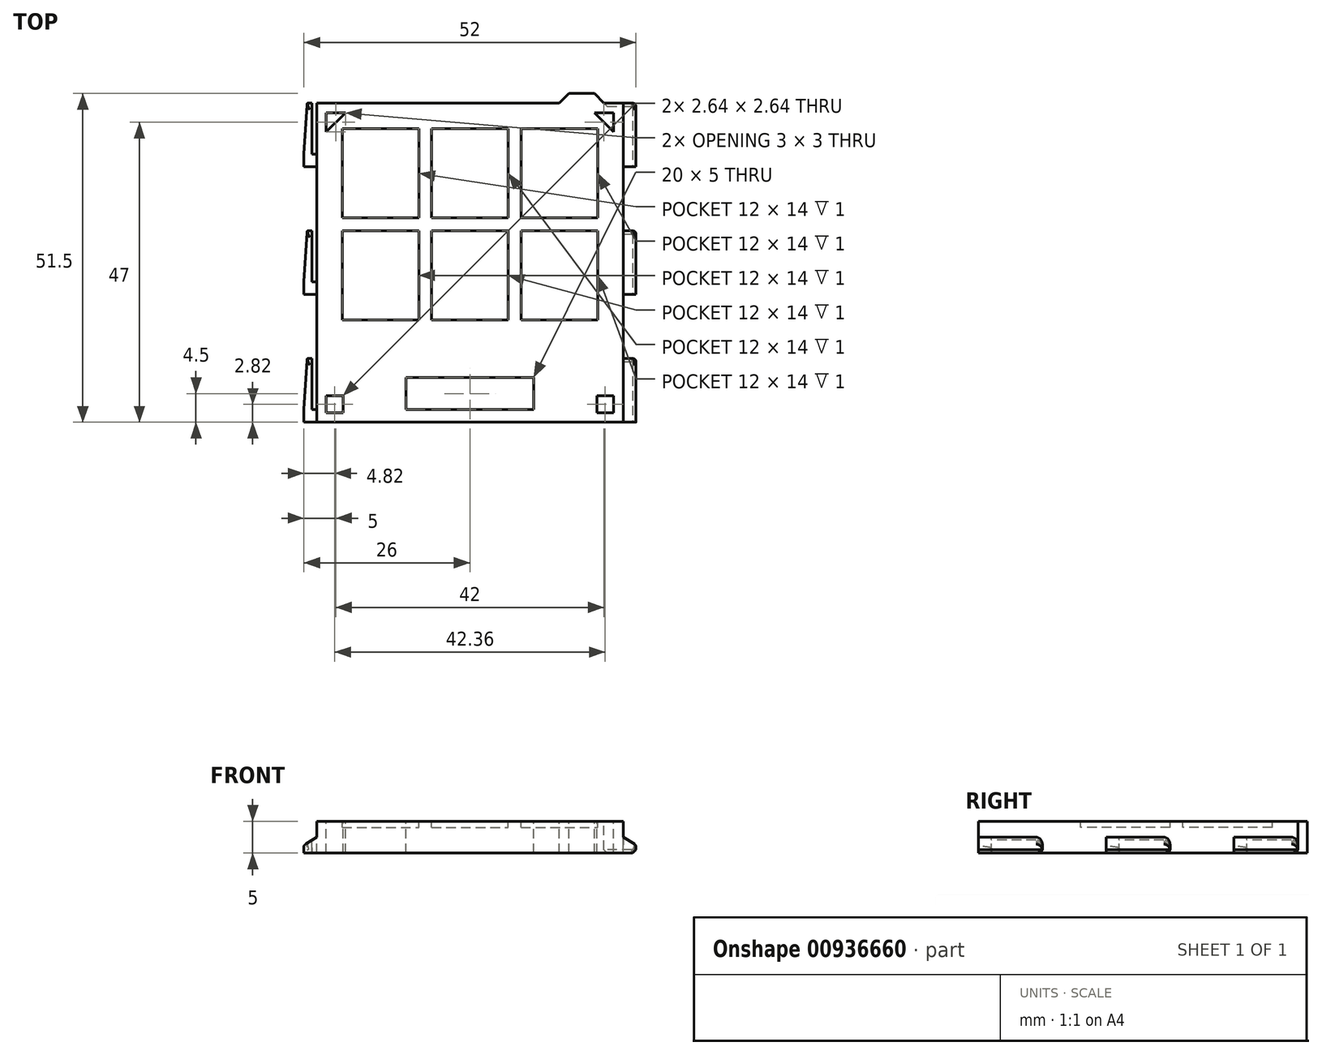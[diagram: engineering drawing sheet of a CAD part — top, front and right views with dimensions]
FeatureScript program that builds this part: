
annotation { "Feature Type Name" : "Feature", "Feature Type Description" : "" }
export const myFeature = defineFeature(function(context is Context, id is Id, definition is map)
    precondition{}
    {
        {
            var Q0;
            Q0=qCreatedBy(makeId("Top.planeOp"),FACE);
            var sketch = newSketch(context, id + "F0", { "sketchPlane" : qUnion([Q0])});
            skLineSegment(sketch, "E0.bottom", {"start": v(0, 0) * mm, "end": v(48, 0) * mm});
            skLineSegment(sketch, "E0.top", {"start": v(0, -50) * mm, "end": v(48, -50) * mm});
            skLineSegment(sketch, "E0.left", {"start": v(0, 0) * mm, "end": v(0, -50) * mm});
            skLineSegment(sketch, "E0.right", {"start": v(48, 0) * mm, "end": v(48, -50) * mm});
            skSolve(sketch);
        }
        {
            var Q0;
            Q0=makeQuery(id+"F0.imprint","IMPRINT",FACE,{"disambiguationData":[TD([[makeQuery(id+"F0.imprint","IMPRINT",EDGE,{"derivedFrom":sQuery(id+"F0.wireOp",EDGE,"E0.bottom")}),-1.0]])]});
            extrude(context, id + "F1", {"entities" : qUnion([Q0]), "depth" : 5 * mm, "offsetDistance" : 25 * mm});
        }
        {
            var Q0;
            Q0=makeQuery(id+"F1.opExtrude","CAP_FACE",FACE,{"disambiguationData":[OSD([sQuery(id+"F0.wireOp",EDGE,"E0.bottom"),sQuery(id+"F0.wireOp",EDGE,"E0.top"),sQuery(id+"F0.wireOp",EDGE,"E0.left"),sQuery(id+"F0.wireOp",EDGE,"E0.right")])],"isStart":false});
            var sketch = newSketch(context, id + "F2", { "sketchPlane" : qUnion([Q0])});
            skLineSegment(sketch, "E1.bottom", {"start": v(4, -4) * mm, "end": v(16, -4) * mm});
            skLineSegment(sketch, "E1.top", {"start": v(4, -18) * mm, "end": v(16, -18) * mm});
            skLineSegment(sketch, "E1.left", {"start": v(4, -4) * mm, "end": v(4, -18) * mm});
            skLineSegment(sketch, "E1.right", {"start": v(16, -4) * mm, "end": v(16, -18) * mm});
            skLineSegment(sketch, "E2.0.1.0", {"start": v(4, -34) * mm, "end": v(16, -34) * mm});
            skLineSegment(sketch, "E2.0.1.1", {"start": v(16, -20) * mm, "end": v(16, -34) * mm});
            skLineSegment(sketch, "E2.0.1.2", {"start": v(4, -20) * mm, "end": v(4, -34) * mm});
            skLineSegment(sketch, "E2.0.1.3", {"start": v(4, -20) * mm, "end": v(16, -20) * mm});
            skLineSegment(sketch, "E2.1.0.0", {"start": v(18, -18) * mm, "end": v(30, -18) * mm});
            skLineSegment(sketch, "E2.1.0.1", {"start": v(30, -4) * mm, "end": v(30, -18) * mm});
            skLineSegment(sketch, "E2.1.0.2", {"start": v(18, -4) * mm, "end": v(18, -18) * mm});
            skLineSegment(sketch, "E2.1.0.3", {"start": v(18, -4) * mm, "end": v(30, -4) * mm});
            skLineSegment(sketch, "E2.1.1.0", {"start": v(18, -34) * mm, "end": v(30, -34) * mm});
            skLineSegment(sketch, "E2.1.1.1", {"start": v(30, -20) * mm, "end": v(30, -34) * mm});
            skLineSegment(sketch, "E2.1.1.2", {"start": v(18, -20) * mm, "end": v(18, -34) * mm});
            skLineSegment(sketch, "E2.1.1.3", {"start": v(18, -20) * mm, "end": v(30, -20) * mm});
            skLineSegment(sketch, "E2.direction1", {"start": v(4, -18) * mm, "end": v(18, -18) * mm, "construction": true});
            skLineSegment(sketch, "E2.direction2", {"start": v(4, -18) * mm, "end": v(4, -34) * mm, "construction": true});
            skLineSegment(sketch, "E3.0.2.0", {"start": v(32, -18) * mm, "end": v(44, -18) * mm});
            skLineSegment(sketch, "E3.3.2.0", {"start": v(44, -4) * mm, "end": v(44, -18) * mm});
            skLineSegment(sketch, "E3.6.2.0", {"start": v(32, -4) * mm, "end": v(32, -18) * mm});
            skLineSegment(sketch, "E3.9.2.0", {"start": v(32, -4) * mm, "end": v(44, -4) * mm});
            skLineSegment(sketch, "E3.0.2.1", {"start": v(32, -34) * mm, "end": v(44, -34) * mm});
            skLineSegment(sketch, "E3.3.2.1", {"start": v(44, -20) * mm, "end": v(44, -34) * mm});
            skLineSegment(sketch, "E3.6.2.1", {"start": v(32, -20) * mm, "end": v(32, -34) * mm});
            skLineSegment(sketch, "E3.9.2.1", {"start": v(32, -20) * mm, "end": v(44, -20) * mm});
            skSolve(sketch);
        }
        {
            var Q0;
            Q0=makeQuery(id+"F2.imprint","IMPRINT",FACE,{"disambiguationData":[TD([[makeQuery(id+"F2.imprint","IMPRINT",EDGE,{"derivedFrom":sQuery(id+"F2.wireOp",EDGE,"E1.bottom")}),-1.0]])]});
            var Q1;
            Q1=makeQuery(id+"F2.imprint","IMPRINT",FACE,{"disambiguationData":[TD([[makeQuery(id+"F2.imprint","IMPRINT",EDGE,{"derivedFrom":sQuery(id+"F2.wireOp",EDGE,"E2.0.1.0")}),1.0]])]});
            var Q2;
            Q2=makeQuery(id+"F2.imprint","IMPRINT",FACE,{"disambiguationData":[TD([[makeQuery(id+"F2.imprint","IMPRINT",EDGE,{"derivedFrom":sQuery(id+"F2.wireOp",EDGE,"E2.0.2.0")}),1.0]])]});
            var Q3;
            Q3=makeQuery(id+"F2.imprint","IMPRINT",FACE,{"disambiguationData":[TD([[makeQuery(id+"F2.imprint","IMPRINT",EDGE,{"derivedFrom":sQuery(id+"F2.wireOp",EDGE,"E2.0.3.0")}),1.0]])]});
            var Q4;
            Q4=makeQuery(id+"F2.imprint","IMPRINT",FACE,{"disambiguationData":[TD([[makeQuery(id+"F2.imprint","IMPRINT",EDGE,{"derivedFrom":sQuery(id+"F2.wireOp",EDGE,"E2.2.0.0")}),1.0]])]});
            var Q5;
            Q5=makeQuery(id+"F2.imprint","IMPRINT",FACE,{"disambiguationData":[TD([[makeQuery(id+"F2.imprint","IMPRINT",EDGE,{"derivedFrom":sQuery(id+"F2.wireOp",EDGE,"E2.2.1.0")}),1.0]])]});
            var Q6;
            Q6=makeQuery(id+"F2.imprint","IMPRINT",FACE,{"disambiguationData":[TD([[makeQuery(id+"F2.imprint","IMPRINT",EDGE,{"derivedFrom":sQuery(id+"F2.wireOp",EDGE,"E2.2.2.0")}),1.0]])]});
            var Q7;
            Q7=makeQuery(id+"F2.imprint","IMPRINT",FACE,{"disambiguationData":[TD([[makeQuery(id+"F2.imprint","IMPRINT",EDGE,{"derivedFrom":sQuery(id+"F2.wireOp",EDGE,"E2.4.3.0")}),1.0]])]});
            var Q8;
            Q8=makeQuery(id+"F2.imprint","IMPRINT",FACE,{"disambiguationData":[TD([[makeQuery(id+"F2.imprint","IMPRINT",EDGE,{"derivedFrom":sQuery(id+"F2.wireOp",EDGE,"E2.4.4.0")}),1.0]])]});
            var Q9;
            Q9=makeQuery(id+"F2.imprint","IMPRINT",FACE,{"disambiguationData":[TD([[makeQuery(id+"F2.imprint","IMPRINT",EDGE,{"derivedFrom":sQuery(id+"F2.wireOp",EDGE,"E2.4.5.0")}),1.0]])]});
            var Q10;
            Q10=makeQuery(id+"F2.imprint","IMPRINT",FACE,{"disambiguationData":[TD([[makeQuery(id+"F2.imprint","IMPRINT",EDGE,{"derivedFrom":sQuery(id+"F2.wireOp",EDGE,"E2.5.0.0")}),1.0]])]});
            var Q11;
            Q11=makeQuery(id+"F2.imprint","IMPRINT",FACE,{"disambiguationData":[TD([[makeQuery(id+"F2.imprint","IMPRINT",EDGE,{"derivedFrom":sQuery(id+"F2.wireOp",EDGE,"E2.5.1.0")}),1.0]])]});
            var Q12;
            Q12=makeQuery(id+"F2.imprint","IMPRINT",FACE,{"disambiguationData":[TD([[makeQuery(id+"F2.imprint","IMPRINT",EDGE,{"derivedFrom":sQuery(id+"F2.wireOp",EDGE,"E2.5.2.0")}),1.0]])]});
            var Q13;
            Q13=makeQuery(id+"F2.imprint","IMPRINT",FACE,{"disambiguationData":[TD([[makeQuery(id+"F2.imprint","IMPRINT",EDGE,{"derivedFrom":sQuery(id+"F2.wireOp",EDGE,"E2.5.5.0")}),1.0]])]});
            var Q14;
            Q14=makeQuery(id+"F2.imprint","IMPRINT",FACE,{"disambiguationData":[TD([[makeQuery(id+"F2.imprint","IMPRINT",EDGE,{"derivedFrom":sQuery(id+"F2.wireOp",EDGE,"E2.5.4.0")}),1.0]])]});
            var Q15;
            Q15=makeQuery(id+"F2.imprint","IMPRINT",FACE,{"disambiguationData":[TD([[makeQuery(id+"F2.imprint","IMPRINT",EDGE,{"derivedFrom":sQuery(id+"F2.wireOp",EDGE,"E2.5.3.0")}),1.0]])]});
            var Q16;
            Q16=makeQuery(id+"F2.imprint","IMPRINT",FACE,{"disambiguationData":[TD([[makeQuery(id+"F2.imprint","IMPRINT",EDGE,{"derivedFrom":sQuery(id+"F2.wireOp",EDGE,"E2.4.2.0")}),1.0]])]});
            var Q17;
            Q17=makeQuery(id+"F2.imprint","IMPRINT",FACE,{"disambiguationData":[TD([[makeQuery(id+"F2.imprint","IMPRINT",EDGE,{"derivedFrom":sQuery(id+"F2.wireOp",EDGE,"E2.4.1.0")}),1.0]])]});
            var Q18;
            Q18=makeQuery(id+"F2.imprint","IMPRINT",FACE,{"disambiguationData":[TD([[makeQuery(id+"F2.imprint","IMPRINT",EDGE,{"derivedFrom":sQuery(id+"F2.wireOp",EDGE,"E2.4.0.0")}),1.0]])]});
            var Q19;
            Q19=makeQuery(id+"F2.imprint","IMPRINT",FACE,{"disambiguationData":[TD([[makeQuery(id+"F2.imprint","IMPRINT",EDGE,{"derivedFrom":sQuery(id+"F2.wireOp",EDGE,"E2.3.5.0")}),1.0]])]});
            var Q20;
            Q20=makeQuery(id+"F2.imprint","IMPRINT",FACE,{"disambiguationData":[TD([[makeQuery(id+"F2.imprint","IMPRINT",EDGE,{"derivedFrom":sQuery(id+"F2.wireOp",EDGE,"E2.3.4.0")}),1.0]])]});
            var Q21;
            Q21=makeQuery(id+"F2.imprint","IMPRINT",FACE,{"disambiguationData":[TD([[makeQuery(id+"F2.imprint","IMPRINT",EDGE,{"derivedFrom":sQuery(id+"F2.wireOp",EDGE,"E2.3.3.0")}),1.0]])]});
            var Q22;
            Q22=makeQuery(id+"F2.imprint","IMPRINT",FACE,{"disambiguationData":[TD([[makeQuery(id+"F2.imprint","IMPRINT",EDGE,{"derivedFrom":sQuery(id+"F2.wireOp",EDGE,"E2.3.2.0")}),1.0]])]});
            var Q23;
            Q23=makeQuery(id+"F2.imprint","IMPRINT",FACE,{"disambiguationData":[TD([[makeQuery(id+"F2.imprint","IMPRINT",EDGE,{"derivedFrom":sQuery(id+"F2.wireOp",EDGE,"E2.3.1.0")}),1.0]])]});
            var Q24;
            Q24=makeQuery(id+"F2.imprint","IMPRINT",FACE,{"disambiguationData":[TD([[makeQuery(id+"F2.imprint","IMPRINT",EDGE,{"derivedFrom":sQuery(id+"F2.wireOp",EDGE,"E2.3.0.0")}),1.0]])]});
            var Q25;
            Q25=makeQuery(id+"F2.imprint","IMPRINT",FACE,{"disambiguationData":[TD([[makeQuery(id+"F2.imprint","IMPRINT",EDGE,{"derivedFrom":sQuery(id+"F2.wireOp",EDGE,"E2.2.5.0")}),1.0]])]});
            var Q26;
            Q26=makeQuery(id+"F2.imprint","IMPRINT",FACE,{"disambiguationData":[TD([[makeQuery(id+"F2.imprint","IMPRINT",EDGE,{"derivedFrom":sQuery(id+"F2.wireOp",EDGE,"E2.2.4.0")}),1.0]])]});
            var Q27;
            Q27=makeQuery(id+"F2.imprint","IMPRINT",FACE,{"disambiguationData":[TD([[makeQuery(id+"F2.imprint","IMPRINT",EDGE,{"derivedFrom":sQuery(id+"F2.wireOp",EDGE,"E2.1.5.0")}),1.0]])]});
            var Q28;
            Q28=makeQuery(id+"F2.imprint","IMPRINT",FACE,{"disambiguationData":[TD([[makeQuery(id+"F2.imprint","IMPRINT",EDGE,{"derivedFrom":sQuery(id+"F2.wireOp",EDGE,"E2.0.5.0")}),1.0]])]});
            var Q29;
            Q29=makeQuery(id+"F2.imprint","IMPRINT",FACE,{"disambiguationData":[TD([[makeQuery(id+"F2.imprint","IMPRINT",EDGE,{"derivedFrom":sQuery(id+"F2.wireOp",EDGE,"E2.0.4.0")}),1.0]])]});
            var Q30;
            Q30=makeQuery(id+"F2.imprint","IMPRINT",FACE,{"disambiguationData":[TD([[makeQuery(id+"F2.imprint","IMPRINT",EDGE,{"derivedFrom":sQuery(id+"F2.wireOp",EDGE,"E2.1.4.0")}),1.0]])]});
            var Q31;
            Q31=makeQuery(id+"F2.imprint","IMPRINT",FACE,{"disambiguationData":[TD([[makeQuery(id+"F2.imprint","IMPRINT",EDGE,{"derivedFrom":sQuery(id+"F2.wireOp",EDGE,"E2.1.3.0")}),1.0]])]});
            var Q32;
            Q32=makeQuery(id+"F2.imprint","IMPRINT",FACE,{"disambiguationData":[TD([[makeQuery(id+"F2.imprint","IMPRINT",EDGE,{"derivedFrom":sQuery(id+"F2.wireOp",EDGE,"E2.2.3.0")}),1.0]])]});
            var Q33;
            Q33=makeQuery(id+"F2.imprint","IMPRINT",FACE,{"disambiguationData":[TD([[makeQuery(id+"F2.imprint","IMPRINT",EDGE,{"derivedFrom":sQuery(id+"F2.wireOp",EDGE,"E2.1.2.0")}),1.0]])]});
            var Q34;
            Q34=makeQuery(id+"F2.imprint","IMPRINT",FACE,{"disambiguationData":[TD([[makeQuery(id+"F2.imprint","IMPRINT",EDGE,{"derivedFrom":sQuery(id+"F2.wireOp",EDGE,"E2.1.1.0")}),1.0]])]});
            var Q35;
            Q35=makeQuery(id+"F2.imprint","IMPRINT",FACE,{"disambiguationData":[TD([[makeQuery(id+"F2.imprint","IMPRINT",EDGE,{"derivedFrom":sQuery(id+"F2.wireOp",EDGE,"E2.1.0.0")}),1.0]])]});
            var Q36;
            Q36=makeQuery(id+"F2.imprint","IMPRINT",FACE,{"disambiguationData":[TD([[makeQuery(id+"F2.imprint","IMPRINT",EDGE,{"derivedFrom":sQuery(id+"F2.wireOp",EDGE,"ff7fc922-6515-4e56-a79b-3e4ea8dee818.0.0.2")}),1.0]])]});
            var Q37;
            Q37=makeQuery(id+"F2.imprint","IMPRINT",FACE,{"disambiguationData":[TD([[makeQuery(id+"F2.imprint","IMPRINT",EDGE,{"derivedFrom":sQuery(id+"F2.wireOp",EDGE,"ff7fc922-6515-4e56-a79b-3e4ea8dee818.0.1.2")}),1.0]])]});
            var Q38;
            Q38=makeQuery(id+"F2.imprint","IMPRINT",FACE,{"disambiguationData":[TD([[makeQuery(id+"F2.imprint","IMPRINT",EDGE,{"derivedFrom":sQuery(id+"F2.wireOp",EDGE,"ff7fc922-6515-4e56-a79b-3e4ea8dee818.0.2.2")}),1.0]])]});
            var Q39;
            Q39=makeQuery(id+"F2.imprint","IMPRINT",FACE,{"disambiguationData":[TD([[makeQuery(id+"F2.imprint","IMPRINT",EDGE,{"derivedFrom":sQuery(id+"F2.wireOp",EDGE,"E3.0.2.1")}),1.0]])]});
            var Q40;
            Q40=makeQuery(id+"F2.imprint","IMPRINT",FACE,{"disambiguationData":[TD([[makeQuery(id+"F2.imprint","IMPRINT",EDGE,{"derivedFrom":sQuery(id+"F2.wireOp",EDGE,"E3.0.2.0")}),1.0]])]});
            extrude(context, id + "F3", {"entities" : qUnion([Q0, Q1, Q2, Q3, Q4, Q5, Q6, Q7, Q8, Q9, Q10, Q11, Q12, Q13, Q14, Q15, Q16, Q17, Q18, Q19, Q20, Q21, Q22, Q23, Q24, Q25, Q26, Q27, Q28, Q29, Q30, Q31, Q32, Q33, Q34, Q35, Q36, Q37, Q38, Q39, Q40]), "operationType" : NewBodyOperationType.REMOVE, "oppositeDirection" : true, "depth" : 1 * mm, "offsetDistance" : 25 * mm});
        }
        {
            var Q0;
            Q0=makeQuery(id+"F1.opExtrude","SWEPT_FACE",FACE,{"disambiguationData":[OSD([sQuery(id+"F0.wireOp",EDGE,"E0.top")])]});
            var sketch = newSketch(context, id + "F4", { "sketchPlane" : qUnion([Q0])});
            skLineSegment(sketch, "E4", {"start": v(0, 0) * mm, "end": v(-2, 0) * mm});
            skLineSegment(sketch, "E5", {"start": v(48, 0) * mm, "end": v(50, 0) * mm});
            skLineSegment(sketch, "E6", {"start": v(50, 0) * mm, "end": v(50, 1.25) * mm});
            skLineSegment(sketch, "E7", {"start": v(50, 1.25) * mm, "end": v(48, 2.5) * mm});
            skLineSegment(sketch, "E8", {"start": v(-2, 0) * mm, "end": v(-2, 1.25) * mm});
            skLineSegment(sketch, "E9", {"start": v(-2, 1.25) * mm, "end": v(0, 2.5) * mm});
            skSolve(sketch);
        }
        {
            var Q0;
            {var subQ6=sQuery(id+"F4.wireOp",EDGE,"E4");Q0=makeQuery(id+"F4.imprint","IMPRINT",FACE,{"disambiguationData":[TD([[makeQuery(id+"F4.imprint","IMPRINT",EDGE,{"derivedFrom":subQ6}),-1.0]])]});}
            var Q1;
            {var subQ1=sQuery(id+"F4.wireOp",EDGE,"E5");Q1=makeQuery(id+"F4.imprint","IMPRINT",FACE,{"disambiguationData":[TD([[makeQuery(id+"F4.imprint","IMPRINT",EDGE,{"derivedFrom":subQ1}),1.0]])]});}
            var Q2;
            Q2=makeQuery(id+"F1.opExtrude","SWEPT_FACE",FACE,{"disambiguationData":[OSD([sQuery(id+"F0.wireOp",EDGE,"E0.bottom")])]});
            extrude(context, id + "F5", {"entities" : qUnion([Q0, Q1]), "operationType" : NewBodyOperationType.ADD, "endBound" : BoundingType.UP_TO_SURFACE, "oppositeDirection" : true, "depth" : 25 * mm, "endBoundEntityFace" : qUnion([Q2]), "offsetDistance" : 25 * mm});
        }
        {
            var Q0;
            Q0=makeQuery(id+"F1.opExtrude","CAP_FACE",FACE,{"disambiguationData":[OSD([sQuery(id+"F0.wireOp",EDGE,"E0.bottom"),sQuery(id+"F0.wireOp",EDGE,"E0.top"),sQuery(id+"F0.wireOp",EDGE,"E0.left"),sQuery(id+"F0.wireOp",EDGE,"E0.right")])],"isStart":false});
            var sketch = newSketch(context, id + "F6", { "sketchPlane" : qUnion([Q0])});
            skPoint(sketch, "E10.firstSnap0", {"position": v(18.5, -4) * mm});
            skLineSegment(sketch, "E10.bottom", {"start": v(0, -10) * mm, "end": v(-6.52, -10) * mm});
            skLineSegment(sketch, "E10.top", {"start": v(0, -20) * mm, "end": v(-6.52, -20) * mm});
            skLineSegment(sketch, "E10.left", {"start": v(0, -10) * mm, "end": v(0, -20) * mm});
            skLineSegment(sketch, "E10.right", {"start": v(-6.52, -10) * mm, "end": v(-6.52, -20) * mm});
            skLineSegment(sketch, "E11", {"start": v(24, 0) * mm, "end": v(24, 8.51) * mm, "construction": true});
            skLineSegment(sketch, "E12.MirrorCS", {"start": v(48, -10) * mm, "end": v(54.52, -10) * mm});
            skLineSegment(sketch, "E13.MirrorCS", {"start": v(48, -10) * mm, "end": v(48, -20) * mm});
            skLineSegment(sketch, "E14.MirrorCS", {"start": v(48, -20) * mm, "end": v(54.52, -20) * mm});
            skLineSegment(sketch, "E15.MirrorCS", {"start": v(54.52, -10) * mm, "end": v(54.52, -20) * mm});
            skLineSegment(sketch, "E16.0.1.0", {"start": v(-6.52, -30) * mm, "end": v(-6.52, -40) * mm});
            skLineSegment(sketch, "E16.0.1.1", {"start": v(0, -30) * mm, "end": v(-6.52, -30) * mm});
            skLineSegment(sketch, "E16.0.1.2", {"start": v(0, -40) * mm, "end": v(-6.52, -40) * mm});
            skLineSegment(sketch, "E16.0.1.3", {"start": v(0, -30) * mm, "end": v(0, -40) * mm});
            skLineSegment(sketch, "E16.0.1.4", {"start": v(48, -30) * mm, "end": v(54.52, -30) * mm});
            skLineSegment(sketch, "E16.0.1.5", {"start": v(48, -30) * mm, "end": v(48, -40) * mm});
            skLineSegment(sketch, "E16.0.1.6", {"start": v(54.52, -30) * mm, "end": v(54.52, -40) * mm});
            skLineSegment(sketch, "E16.0.1.7", {"start": v(48, -40) * mm, "end": v(54.52, -40) * mm});
            skLineSegment(sketch, "E16.direction1", {"start": v(-6.52, -20) * mm, "end": v(18.48, -20) * mm, "construction": true});
            skLineSegment(sketch, "E16.direction2", {"start": v(-6.52, -20) * mm, "end": v(-6.52, -40) * mm, "construction": true});
            skSolve(sketch);
        }
        {
            var Q0;
            Q0=makeQuery(id+"F6.imprint","IMPRINT",FACE,{"disambiguationData":[TD([[makeQuery(id+"F6.imprint","IMPRINT",EDGE,{"derivedFrom":sQuery(id+"F6.wireOp",EDGE,"E10.bottom")}),1.0]])]});
            var Q1;
            Q1=makeQuery(id+"F6.imprint","IMPRINT",FACE,{"disambiguationData":[TD([[makeQuery(id+"F6.imprint","IMPRINT",EDGE,{"derivedFrom":sQuery(id+"F6.wireOp",EDGE,"E16.0.1.0")}),1.0]])]});
            var Q2;
            Q2=makeQuery(id+"F6.imprint","IMPRINT",FACE,{"disambiguationData":[TD([[makeQuery(id+"F6.imprint","IMPRINT",EDGE,{"derivedFrom":sQuery(id+"F6.wireOp",EDGE,"E16.0.1.4")}),-1.0]])]});
            var Q3;
            Q3=makeQuery(id+"F6.imprint","IMPRINT",FACE,{"disambiguationData":[TD([[makeQuery(id+"F6.imprint","IMPRINT",EDGE,{"derivedFrom":sQuery(id+"F6.wireOp",EDGE,"E12.MirrorCS")}),-1.0]])]});
            extrude(context, id + "F7", {"entities" : qUnion([Q0, Q1, Q2, Q3]), "operationType" : NewBodyOperationType.REMOVE, "oppositeDirection" : true, "depth" : 25 * mm, "offsetDistance" : 25 * mm});
        }
        {
            var Q0;
            Q0=makeQuery(id+"F1.opExtrude","CAP_FACE",FACE,{"disambiguationData":[OSD([sQuery(id+"F0.wireOp",EDGE,"E0.bottom"),sQuery(id+"F0.wireOp",EDGE,"E0.top"),sQuery(id+"F0.wireOp",EDGE,"E0.left"),sQuery(id+"F0.wireOp",EDGE,"E0.right")])],"isStart":false});
            var sketch = newSketch(context, id + "F8", { "sketchPlane" : qUnion([Q0])});
            skLineSegment(sketch, "E17", {"start": v(0, -48) * mm, "end": v(-0.75, -48) * mm});
            skLineSegment(sketch, "E18", {"start": v(-0.75, -48) * mm, "end": v(-0.75, -39.37) * mm});
            skLineSegment(sketch, "E19", {"start": v(-0.75, -39.37) * mm, "end": v(0, -39.37) * mm});
            skLineSegment(sketch, "E20", {"start": v(0, -39.37) * mm, "end": v(0, -48) * mm});
            skLineSegment(sketch, "E21.0.0", {"start": v(0, -40) * mm, "end": v(-1.31, -40) * mm});
            skLineSegment(sketch, "E21.0.1", {"start": v(-2, -40) * mm, "end": v(-2, -50) * mm});
            skLineSegment(sketch, "E21.0.2", {"start": v(-2, -50) * mm, "end": v(0, -50) * mm});
            skLineSegment(sketch, "E21.0.3", {"start": v(0, -50) * mm, "end": v(0, -40) * mm});
            skLineSegment(sketch, "E22", {"start": v(-2, -40) * mm, "end": v(-2, -47.93) * mm});
            skLineSegment(sketch, "E23", {"start": v(-2, -47.93) * mm, "end": v(-1.51, -40.19) * mm});
            skLineSegment(sketch, "E24", {"start": v(-1.5, -40) * mm, "end": v(-2, -40) * mm});
            skPoint(sketch, "E25.newPointA", {"position": v(-1.5, -40) * mm});
            skPoint(sketch, "E25.newPointB", {"position": v(-2, -40) * mm});
            skArc(sketch, "E25.filletArc", {"start": v(-1.31, -40) * mm, "mid": v(-1.45, -40.05) * mm, "end": v(-1.51, -40.19) * mm});
            skLineSegment(sketch, "E26", {"start": v(-1.31, -40) * mm, "end": v(-1.5, -40) * mm});
            skLineSegment(sketch, "E27.0.1.0", {"start": v(0, -28) * mm, "end": v(-0.75, -28) * mm});
            skLineSegment(sketch, "E27.0.1.1", {"start": v(-0.75, -28) * mm, "end": v(-0.75, -19.37) * mm});
            skLineSegment(sketch, "E27.0.1.2", {"start": v(-0.75, -19.37) * mm, "end": v(0, -19.37) * mm});
            skLineSegment(sketch, "E27.0.1.3", {"start": v(0, -19.37) * mm, "end": v(0, -28) * mm});
            skLineSegment(sketch, "E27.0.1.4", {"start": v(-2, -27.93) * mm, "end": v(-1.51, -20.19) * mm});
            skLineSegment(sketch, "E27.0.1.5", {"start": v(-2, -20) * mm, "end": v(-2, -30) * mm});
            skLineSegment(sketch, "E27.0.1.6", {"start": v(-1.5, -20) * mm, "end": v(-2, -20) * mm});
            skLineSegment(sketch, "E27.0.1.7", {"start": v(-1.31, -20) * mm, "end": v(-1.5, -20) * mm});
            skArc(sketch, "E27.0.1.8", {"start": v(-1.31, -20) * mm, "mid": v(-1.45, -20.05) * mm, "end": v(-1.51, -20.19) * mm});
            skLineSegment(sketch, "E27.0.2.0", {"start": v(0, -8) * mm, "end": v(-0.75, -8) * mm});
            skLineSegment(sketch, "E27.0.2.1", {"start": v(-0.75, -8) * mm, "end": v(-0.75, 0.63) * mm});
            skLineSegment(sketch, "E27.0.2.2", {"start": v(-0.75, 0.63) * mm, "end": v(0, 0.63) * mm});
            skLineSegment(sketch, "E27.0.2.3", {"start": v(0, 0.63) * mm, "end": v(0, -8) * mm});
            skLineSegment(sketch, "E27.0.2.4", {"start": v(-2, -7.93) * mm, "end": v(-1.51, -0.19) * mm});
            skLineSegment(sketch, "E27.0.2.5", {"start": v(-2, 0) * mm, "end": v(-2, -10) * mm});
            skLineSegment(sketch, "E27.0.2.6", {"start": v(-1.5, 0) * mm, "end": v(-2, 0) * mm});
            skLineSegment(sketch, "E27.0.2.7", {"start": v(-1.31, 0) * mm, "end": v(-1.5, 0) * mm});
            skArc(sketch, "E27.0.2.8", {"start": v(-1.31, 0) * mm, "mid": v(-1.45, -0.05) * mm, "end": v(-1.51, -0.19) * mm});
            skLineSegment(sketch, "E27.direction1", {"start": v(-0.75, -48) * mm, "end": v(24.25, -48) * mm, "construction": true});
            skLineSegment(sketch, "E27.direction2", {"start": v(-0.75, -48) * mm, "end": v(-0.75, -28) * mm, "construction": true});
            skLineSegment(sketch, "E28", {"start": v(24, 0.28) * mm, "end": v(24, 4.26) * mm, "construction": true});
            skPoint(sketch, "E28.startSnap0", {"position": v(24, 0) * mm});
            skSolve(sketch);
        }
        {
            var Q0;
            {var subQ0=sQuery(id+"F8.wireOp",EDGE,"E17");Q0=makeQuery(id+"F8.imprint","IMPRINT",FACE,{"disambiguationData":[TD([[makeQuery(id+"F8.imprint","IMPRINT",EDGE,{"derivedFrom":subQ0}),-1.0]])]});}
            var Q1;
            {var subQ0=sQuery(id+"F8.wireOp",EDGE,"E23");Q1=makeQuery(id+"F8.imprint","IMPRINT",FACE,{"disambiguationData":[TD([[makeQuery(id+"F8.imprint","IMPRINT",EDGE,{"derivedFrom":subQ0}),1.0]])]});}
            var Q2;
            Q2=makeQuery(id+"F8.imprint","IMPRINT",FACE,{"disambiguationData":[TD([[makeQuery(id+"F8.imprint","IMPRINT",EDGE,{"derivedFrom":sQuery(id+"F8.wireOp",EDGE,"E27.0.1.0")}),-1.0]])]});
            var Q3;
            {var subQ2=sQuery(id+"F8.wireOp",EDGE,"E27.0.1.4");Q3=makeQuery(id+"F8.imprint","IMPRINT",FACE,{"disambiguationData":[TD([[makeQuery(id+"F8.imprint","IMPRINT",EDGE,{"derivedFrom":subQ2}),1.0]])]});}
            var Q4;
            {var subQ2=sQuery(id+"F8.wireOp",EDGE,"E27.0.2.0");Q4=makeQuery(id+"F8.imprint","IMPRINT",FACE,{"disambiguationData":[TD([[makeQuery(id+"F8.imprint","IMPRINT",EDGE,{"derivedFrom":subQ2}),-1.0]])]});}
            var Q5;
            {var subQ2=sQuery(id+"F8.wireOp",EDGE,"E27.0.2.4");Q5=makeQuery(id+"F8.imprint","IMPRINT",FACE,{"disambiguationData":[TD([[makeQuery(id+"F8.imprint","IMPRINT",EDGE,{"derivedFrom":subQ2}),1.0]])]});}
            var Q6;
            Q6=makeQuery(id+"F8.imprint","IMPRINT",FACE,{"disambiguationData":[TD([[makeQuery(id+"F8.imprint","IMPRINT",EDGE,{"derivedFrom":sQuery(id+"F8.wireOp",EDGE,"e722379a-86f4-49ad-8a47-400355817b230.MirrorCS")}),1.0]])]});
            var Q7;
            Q7=makeQuery(id+"F8.imprint","IMPRINT",FACE,{"disambiguationData":[TD([[makeQuery(id+"F8.imprint","IMPRINT",EDGE,{"derivedFrom":sQuery(id+"F8.wireOp",EDGE,"d30c6836-2050-4577-9a9b-d798b92a200c0.MirrorCS")}),1.0]])]});
            var Q8;
            {var subQ2=sQuery(id+"F8.wireOp",EDGE,"4f4df0a9-7241-4b6c-b748-03f40ba930e40.MirrorCS");Q8=makeQuery(id+"F8.imprint","IMPRINT",FACE,{"disambiguationData":[TD([[makeQuery(id+"F8.imprint","IMPRINT",EDGE,{"derivedFrom":subQ2}),-1.0]])]});}
            var Q9;
            {var subQ1=sQuery(id+"F8.wireOp",EDGE,"5faf99e5-6c72-46fc-adc3-d1651bd9a6770.MirrorCS");Q9=makeQuery(id+"F8.imprint","IMPRINT",FACE,{"disambiguationData":[TD([[makeQuery(id+"F8.imprint","IMPRINT",EDGE,{"derivedFrom":subQ1}),-1.0]])]});}
            var Q10;
            Q10=makeQuery(id+"F8.imprint","IMPRINT",FACE,{"disambiguationData":[TD([[makeQuery(id+"F8.imprint","IMPRINT",EDGE,{"derivedFrom":sQuery(id+"F8.wireOp",EDGE,"cc6e77a2-de85-4070-afac-088a45ef221d0.MirrorCS")}),1.0]])]});
            var Q11;
            Q11=makeQuery(id+"F8.imprint","IMPRINT",FACE,{"disambiguationData":[TD([[makeQuery(id+"F8.imprint","IMPRINT",EDGE,{"derivedFrom":sQuery(id+"F8.wireOp",EDGE,"fa48c959-6260-4dcb-aed2-700d904f25cb0.MirrorCS")}),1.0]])]});
            extrude(context, id + "F9", {"entities" : qUnion([Q0, Q1, Q2, Q3, Q4, Q5, Q6, Q7, Q8, Q9, Q10, Q11]), "operationType" : NewBodyOperationType.REMOVE, "oppositeDirection" : true, "depth" : 25 * mm, "offsetDistance" : 25 * mm});
        }
        {
            var Q0;
            Q0=makeQuery(id+"F7.boolean.opBoolean","INTERSECT",EDGE,{"derivedFrom":[makeQuery(id+"F5.opExtrude","SWEPT_FACE",FACE,{"disambiguationData":[OSD([sQuery(id+"F4.wireOp",EDGE,"E9")])]}),makeQuery(id+"F7.opExtrude","SWEPT_FACE",FACE,{"disambiguationData":[OSD([sQuery(id+"F6.wireOp",EDGE,"E16.0.1.2")])]})]});
            var Q1;
            Q1=makeQuery(id+"F7.boolean.opBoolean","INTERSECT",EDGE,{"derivedFrom":[makeQuery(id+"F5.opExtrude","SWEPT_FACE",FACE,{"disambiguationData":[OSD([sQuery(id+"F4.wireOp",EDGE,"E9")])]}),makeQuery(id+"F7.opExtrude","SWEPT_FACE",FACE,{"disambiguationData":[OSD([sQuery(id+"F6.wireOp",EDGE,"E10.top")])]})]});
            var Q2;
            Q2=makeQuery(id+"F5.opExtrude","CAP_EDGE",EDGE,{"disambiguationData":[OSD([sQuery(id+"F4.wireOp",EDGE,"E9")])],"isStart":false});
            var Q3;
            Q3=makeQuery(id+"F5.opExtrude","CAP_EDGE",EDGE,{"disambiguationData":[OSD([sQuery(id+"F4.wireOp",EDGE,"E7")])],"isStart":false});
            var Q4;
            Q4=makeQuery(id+"F7.boolean.opBoolean","INTERSECT",EDGE,{"derivedFrom":[makeQuery(id+"F5.opExtrude","SWEPT_FACE",FACE,{"disambiguationData":[OSD([sQuery(id+"F4.wireOp",EDGE,"E7")])]}),makeQuery(id+"F7.opExtrude","SWEPT_FACE",FACE,{"disambiguationData":[OSD([sQuery(id+"F6.wireOp",EDGE,"E14.MirrorCS")])]})]});
            var Q5;
            Q5=makeQuery(id+"F7.boolean.opBoolean","INTERSECT",EDGE,{"derivedFrom":[makeQuery(id+"F5.opExtrude","SWEPT_FACE",FACE,{"disambiguationData":[OSD([sQuery(id+"F4.wireOp",EDGE,"E7")])]}),makeQuery(id+"F7.opExtrude","SWEPT_FACE",FACE,{"disambiguationData":[OSD([sQuery(id+"F6.wireOp",EDGE,"E16.0.1.7")])]})]});
            fillet(context, id + "F10", {"entities" : qUnion([Q0, Q1, Q2, Q3, Q4, Q5]), "radius" : 1 * mm, "tangentPropagation" : true, "allowEdgeOverflow" : false});
        }
        {
            var Q0;
            Q0=makeQuery(id+"F1.opExtrude","CAP_FACE",FACE,{"disambiguationData":[OSD([sQuery(id+"F0.wireOp",EDGE,"E0.bottom"),sQuery(id+"F0.wireOp",EDGE,"E0.top"),sQuery(id+"F0.wireOp",EDGE,"E0.left"),sQuery(id+"F0.wireOp",EDGE,"E0.right")])],"isStart":false});
            var sketch = newSketch(context, id + "F11", { "sketchPlane" : qUnion([Q0])});
            skLineSegment(sketch, "E29.bottom", {"start": v(14, -43) * mm, "end": v(34, -43) * mm});
            skLineSegment(sketch, "E29.top", {"start": v(14, -48) * mm, "end": v(34, -48) * mm});
            skLineSegment(sketch, "E29.left", {"start": v(14, -43) * mm, "end": v(14, -48) * mm});
            skLineSegment(sketch, "E29.right", {"start": v(34, -43) * mm, "end": v(34, -48) * mm});
            skLineSegment(sketch, "E30", {"start": v(24, -50) * mm, "end": v(24, -40.68) * mm, "construction": true});
            skPoint(sketch, "E31", {"position": v(24, -48) * mm});
            skLineSegment(sketch, "E32", {"start": v(1.5, -1.5) * mm, "end": v(1.5, -4.5) * mm});
            skLineSegment(sketch, "E33", {"start": v(1.5, -4.5) * mm, "end": v(4.5, -1.5) * mm});
            skLineSegment(sketch, "E34", {"start": v(4.5, -1.5) * mm, "end": v(1.5, -1.5) * mm});
            skLineSegment(sketch, "E35", {"start": v(24, 0) * mm, "end": v(24, -11.18) * mm, "construction": true});
            skLineSegment(sketch, "E36.MirrorCS", {"start": v(46.5, -4.5) * mm, "end": v(43.5, -1.5) * mm});
            skLineSegment(sketch, "E37.MirrorCS", {"start": v(46.5, -1.5) * mm, "end": v(46.5, -4.5) * mm});
            skLineSegment(sketch, "E38.MirrorCS", {"start": v(43.5, -1.5) * mm, "end": v(46.5, -1.5) * mm});
            skLineSegment(sketch, "E39", {"start": v(0, -25) * mm, "end": v(9, -25) * mm, "construction": true});
            skLineSegment(sketch, "E40.MirrorCS", {"start": v(1.5, -45.5) * mm, "end": v(4.5, -48.5) * mm});
            skLineSegment(sketch, "E41.MirrorCS", {"start": v(46.5, -45.5) * mm, "end": v(43.5, -48.5) * mm});
            skLineSegment(sketch, "E42.MirrorCS", {"start": v(43.5, -48.5) * mm, "end": v(46.5, -48.5) * mm});
            skLineSegment(sketch, "E43.MirrorCS", {"start": v(46.5, -48.5) * mm, "end": v(46.5, -45.5) * mm});
            skLineSegment(sketch, "E44.MirrorCS", {"start": v(4.5, -48.5) * mm, "end": v(1.5, -48.5) * mm});
            skLineSegment(sketch, "E45.MirrorCS", {"start": v(1.5, -48.5) * mm, "end": v(1.5, -45.5) * mm});
            skLineSegment(sketch, "E46", {"start": v(1.5, -45.5) * mm, "end": v(4.5, -45.5) * mm});
            skLineSegment(sketch, "E47", {"start": v(4.5, -45.5) * mm, "end": v(4.5, -48.5) * mm});
            skLineSegment(sketch, "E48", {"start": v(46.5, -45.5) * mm, "end": v(43.5, -45.5) * mm});
            skLineSegment(sketch, "E49", {"start": v(43.5, -45.5) * mm, "end": v(43.5, -48.5) * mm});
            skLineSegment(sketch, "E50", {"start": v(1.5, -45.86) * mm, "end": v(4.5, -45.86) * mm});
            skLineSegment(sketch, "E51", {"start": v(4.14, -45.5) * mm, "end": v(4.14, -48.5) * mm});
            skLineSegment(sketch, "E52", {"start": v(43.86, -48.5) * mm, "end": v(43.86, -45.5) * mm});
            skLineSegment(sketch, "E53", {"start": v(43.5, -45.86) * mm, "end": v(46.5, -45.86) * mm});
            skSolve(sketch);
        }
        {
            var Q0;
            Q0=makeQuery(id+"F11.imprint","IMPRINT",FACE,{"disambiguationData":[TD([[makeQuery(id+"F11.imprint","IMPRINT",EDGE,{"derivedFrom":sQuery(id+"F11.wireOp",EDGE,"E29.bottom")}),-1.0]])]});
            var Q1;
            Q1=makeQuery(id+"F11.imprint","IMPRINT",FACE,{"disambiguationData":[TD([[makeQuery(id+"F11.imprint","IMPRINT",EDGE,{"derivedFrom":sQuery(id+"F11.wireOp",EDGE,"E36.MirrorCS")}),-1.0]])]});
            var Q2;
            Q2=makeQuery(id+"F11.imprint","IMPRINT",FACE,{"disambiguationData":[TD([[makeQuery(id+"F11.imprint","IMPRINT",EDGE,{"derivedFrom":sQuery(id+"F11.wireOp",EDGE,"E32")}),1.0]])]});
            var Q3;
            Q3=makeQuery(id+"F11.imprint","IMPRINT",FACE,{"disambiguationData":[TD([[makeQuery(id+"F11.imprint","IMPRINT",EDGE,{"derivedFrom":sQuery(id+"F11.wireOp",EDGE,"E40.MirrorCS")}),1.0]])]});
            var Q4;
            Q4=makeQuery(id+"F11.imprint","IMPRINT",FACE,{"disambiguationData":[TD([[makeQuery(id+"F11.imprint","IMPRINT",EDGE,{"derivedFrom":sQuery(id+"F11.wireOp",EDGE,"E41.MirrorCS")}),-1.0]])]});
            var Q5;
            {var subQ3=sQuery(id+"F11.wireOp",EDGE,"E41.MirrorCS");var subQ7=sQuery(id+"F11.wireOp",EDGE,"E53");var subQ9=makeQuery(id+"F11.imprint","INTERSECT",VERTEX,{"derivedFrom":[subQ3,subQ7]});Q5=makeQuery(id+"F11.imprint","IMPRINT",FACE,{"disambiguationData":[TD([[makeQuery(id+"F11.imprint","IMPRINT",EDGE,{"disambiguationData":[TD([[subQ9,-1.0]])],"derivedFrom":subQ3}),1.0]])]});}
            var Q6;
            {var subQ0=sQuery(id+"F11.wireOp",EDGE,"E50");var subQ3=sQuery(id+"F11.wireOp",EDGE,"E40.MirrorCS");var subQ4=makeQuery(id+"F11.imprint","INTERSECT",VERTEX,{"derivedFrom":[subQ3,subQ0]});Q6=makeQuery(id+"F11.imprint","IMPRINT",FACE,{"disambiguationData":[TD([[makeQuery(id+"F11.imprint","IMPRINT",EDGE,{"disambiguationData":[TD([[subQ4,-1.0]])],"derivedFrom":subQ3}),-1.0]])]});}
            extrude(context, id + "F12", {"entities" : qUnion([Q0, Q1, Q2, Q3, Q4, Q5, Q6]), "operationType" : NewBodyOperationType.REMOVE, "oppositeDirection" : true, "depth" : 5 * mm, "offsetDistance" : 25 * mm});
        }
        {
            var Q0;
            {var subQ0=sQuery(id+"F4.wireOp",EDGE,"E7");var subQ1=sQuery(id+"F4.wireOp",EDGE,"E6");var subQ2=sQuery(id+"F0.wireOp",EDGE,"E0.top");Q0=makeQuery(id+"F7.boolean.opBoolean","SPLIT",EDGE,{"disambiguationData":[TD([makeQuery(id+"F1.opExtrude","SWEPT_FACE",FACE,{"disambiguationData":[OSD([subQ2])]})])],"derivedFrom":makeQuery(id+"F5.opExtrude","SWEPT_EDGE",EDGE,{"disambiguationData":[OSD([subQ1,subQ0])]})});}
            var Q1;
            {var subQ0=sQuery(id+"F4.wireOp",EDGE,"E6");var subQ1=sQuery(id+"F4.wireOp",EDGE,"E7");Q1=makeQuery(id+"F7.boolean.opBoolean","SPLIT",EDGE,{"disambiguationData":[TD([makeQuery(id+"F7.opExtrude","SWEPT_FACE",FACE,{"disambiguationData":[OSD([sQuery(id+"F6.wireOp",EDGE,"E14.MirrorCS")])]})])],"derivedFrom":makeQuery(id+"F5.opExtrude","SWEPT_EDGE",EDGE,{"disambiguationData":[OSD([subQ0,subQ1])]})});}
            var Q2;
            {var subQ0=sQuery(id+"F4.wireOp",EDGE,"E6");var subQ1=sQuery(id+"F4.wireOp",EDGE,"E7");Q2=makeQuery(id+"F7.boolean.opBoolean","SPLIT",EDGE,{"disambiguationData":[TD([makeQuery(id+"F1.opExtrude","SWEPT_FACE",FACE,{"disambiguationData":[OSD([sQuery(id+"F0.wireOp",EDGE,"E0.bottom")])]})])],"derivedFrom":makeQuery(id+"F5.opExtrude","SWEPT_EDGE",EDGE,{"disambiguationData":[OSD([subQ0,subQ1])]})});}
            fillet(context, id + "F13", {"entities" : qUnion([Q0, Q1, Q2]), "radius" : 0.5 * mm, "tangentPropagation" : true, "allowEdgeOverflow" : false});
        }
        {
            var Q0;
            Q0=makeQuery(id+"F1.opExtrude","CAP_FACE",FACE,{"disambiguationData":[OSD([sQuery(id+"F0.wireOp",EDGE,"E0.bottom"),sQuery(id+"F0.wireOp",EDGE,"E0.top"),sQuery(id+"F0.wireOp",EDGE,"E0.left"),sQuery(id+"F0.wireOp",EDGE,"E0.right")])],"isStart":false});
            var sketch = newSketch(context, id + "F14", { "sketchPlane" : qUnion([Q0])});
            skLineSegment(sketch, "E54", {"start": v(45, 0) * mm, "end": v(43.5, 1.5) * mm});
            skLineSegment(sketch, "E55", {"start": v(43.5, 1.5) * mm, "end": v(39.5, 1.5) * mm});
            skLineSegment(sketch, "E56", {"start": v(39.5, 1.5) * mm, "end": v(38, 0) * mm});
            skSolve(sketch);
        }
        {
            var Q0;
            {var subQ0=sQuery(id+"F14.wireOp",EDGE,"E54");Q0=makeQuery(id+"F14.imprint","IMPRINT",FACE,{"disambiguationData":[TD([[makeQuery(id+"F14.imprint","IMPRINT",EDGE,{"derivedFrom":subQ0}),1.0]])]});}
            extrude(context, id + "F15", {"entities" : qUnion([Q0]), "operationType" : NewBodyOperationType.ADD, "oppositeDirection" : true, "depth" : 5 * mm, "offsetDistance" : 25 * mm});
        }
        {
            var Q0;
            {var subQ0=sQuery(id+"F4.wireOp",EDGE,"E6");var subQ1=sQuery(id+"F4.wireOp",EDGE,"E5");Q0=makeQuery(id+"F7.boolean.opBoolean","SPLIT",EDGE,{"disambiguationData":[TD([makeQuery(id+"F7.opExtrude","SWEPT_FACE",FACE,{"disambiguationData":[OSD([sQuery(id+"F6.wireOp",EDGE,"E14.MirrorCS")])]})])],"derivedFrom":makeQuery(id+"F5.opExtrude","SWEPT_EDGE",EDGE,{"disambiguationData":[OSD([subQ1,subQ0])]})});}
            var Q1;
            {var subQ4=sQuery(id+"F0.wireOp",EDGE,"E0.bottom");var subQ5=sQuery(id+"F4.wireOp",EDGE,"E6");var subQ6=sQuery(id+"F4.wireOp",EDGE,"E5");Q1=makeQuery(id+"F7.boolean.opBoolean","SPLIT",EDGE,{"disambiguationData":[TD([makeQuery(id+"F1.opExtrude","SWEPT_FACE",FACE,{"disambiguationData":[OSD([subQ4])]})])],"derivedFrom":makeQuery(id+"F5.opExtrude","SWEPT_EDGE",EDGE,{"disambiguationData":[OSD([subQ6,subQ5])]})});}
            var Q2;
            {var subQ2=sQuery(id+"F0.wireOp",EDGE,"E0.top");var subQ4=sQuery(id+"F4.wireOp",EDGE,"E6");var subQ5=sQuery(id+"F4.wireOp",EDGE,"E5");Q2=makeQuery(id+"F7.boolean.opBoolean","SPLIT",EDGE,{"disambiguationData":[TD([makeQuery(id+"F1.opExtrude","SWEPT_FACE",FACE,{"disambiguationData":[OSD([subQ2])]})])],"derivedFrom":makeQuery(id+"F5.opExtrude","SWEPT_EDGE",EDGE,{"disambiguationData":[OSD([subQ5,subQ4])]})});}
            chamfer(context, id + "F16", {"entities" : qUnion([Q0, Q1, Q2]), "width" : 0.5 * mm, "tangentPropagation" : true});
        }
    });
